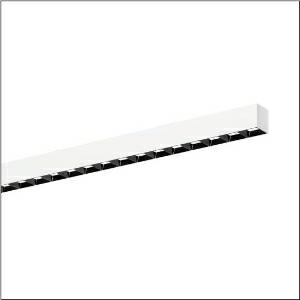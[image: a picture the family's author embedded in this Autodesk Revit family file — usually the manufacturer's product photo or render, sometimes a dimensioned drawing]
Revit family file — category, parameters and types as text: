
# Revit family: silica_21_51mx24da34wb
name_source: partatom
category: Lighting Fixtures
units: mm (PartAtom-declared; Revit-internal decimal feet)

## family parameters
Cut with Voids When Loaded = No
Host = Face
Light Source = No
Part Type = Normal
Room Calculation Point = No
Round Connector Dimension = Use Diameter
Shared = No

## types (1)
- --- (1 x LED, 4320 lm, 32.1 W, 3000K)
    Apparent Load = 32 VA
    CIE Flux Codes = 74 94 99 100 100
    Color Rendering = 80
    Color Temperature = 3000K
    Default Elevation = 1800 mm
    Description = Silica 21, office luminaire, primary light control with darklight reflector, of PMMA, black, CAT 2 (L<= 3000cd/m²), light emission: direct distribution, primary light characteristic: asymmetric, installation type: surface-mounted, LED, rated luminous flux: 4.320lm, luminous efficacy: 135lm/W, light colour: 830, colour temperature: 3000K, control gear: DALI 2, with terminal, 3+2-pole, max. 2.5mm², mains connection: 220..240V, AC, 50/60Hz, rated input power: 32.1W, luminaire housing, of aluminium, traffic white (RAL 9016), length: 1.204mm, width: 53mm, height: 53mm, protection rating (complete): IP20, insulation class (complete): insulation class I (protective earthing), certification: CE, permissible operating ambient temperature: 0..+35°C, standard: EN 50419, packaging unit: 1 piece
    Height = 53 mm
    Lamp = 1 x LED
    Lamp Light Flux = 4320 lm
    Lamp Power = 32.1 W
    Lamp count = 1
    Length = 1204 mm
    Luminous efficacy = 135 lm/W
    Manufacturer = Siteco
    ModVariant = No
    Model = 51MX24DA34WB
    Mounting Place = Ceiling
    Mounting Type = Surface mounted
    Number of Poles = 1
    OnlyDefault = Yes
    Power Factor = 1
    Product Name = Silica 21
    Product group = office luminaire | ceiling mounted
    ProductGroupID = 301
    Protection Class = Protection class I
    Protection Degree = IP 20
    RLX_Detail_Level = 1
    RLX_Emergency_Light_Flux = 0 lm
    RLX_Emergency_Type = 0
    RLX_Emergency_Type_DB = No
    RlxData = <blob elided: 41609 chars, md5=e992dc3d>
    Socket = socket
    Standby Power = 0 W
    System Light Flux = 4320 lm
    System Power = 32 W
    Type Comments = factory setting: luminous flux: 100 % | dim-lin: 254 | 448 mA
    Type Image = l_1335873.jpg
    URL = http://relux.com
    VarID = @adj_123411
    Voltage = 0 V
    Weight = 0.00 kg
    Width = 53 mm

## geometry (parser evidence)
native form markers: Blend x4, Sweep x10
no freeform markers — native parametric forms only
